# Revit family: QF_MOFFAT_BLUESEAL_CE_G580-12
name_source: partatom
category: Specialty Equipment
revit_build: Autodesk Revit Architecture 2012 (Build: 20110916_2132(x64)
units: mm (PartAtom-declared; Revit-internal decimal feet)

## types (1)
- QF_MOFFAT_BLUESEAL_CE_G580-12
    Apparent Power = 230 VA
    Cold Water Connection Height = 0 mm  [stored 0 ft]
    Cold Water Maximum Pressure = 0.00 psi
    Cold Water Minimum Pressure = 0.00 psi
    Cold Water Size = 1"
    Conn Conduit = Yes
    Cycle = 50 Hz
    Description = 1200MM GAS BRATT PAN 120 LITRE WITH MANUAL LIFT
    Elec Conn Connection Height = 0 mm  [stored 0 ft]
    Elec Conn RI Height = 0 mm  [stored 0 ft]
    FL Amps = 1 A
    Manufacturer = MOFFAT BLUESEAL
    Max Overcurrent Protection = 0 A
    Min Ckt Ampacity = 0 A
    Model = G580-12
    Number of Poles = 1
    Phase = 1
    URL = www.moffat.com
    URL Cutsheet = www.moffat.com
    Volts = 230 V
    Watts = 230 W
    Weight in Pounds = 374.8

note: [stored X ft] marks values corroborated as IEEE doubles in the binary element streams (Revit-internal decimal feet)

## geometry (parser evidence)
native form markers: Blend x7, Sweep x8
no freeform markers — native parametric forms only
